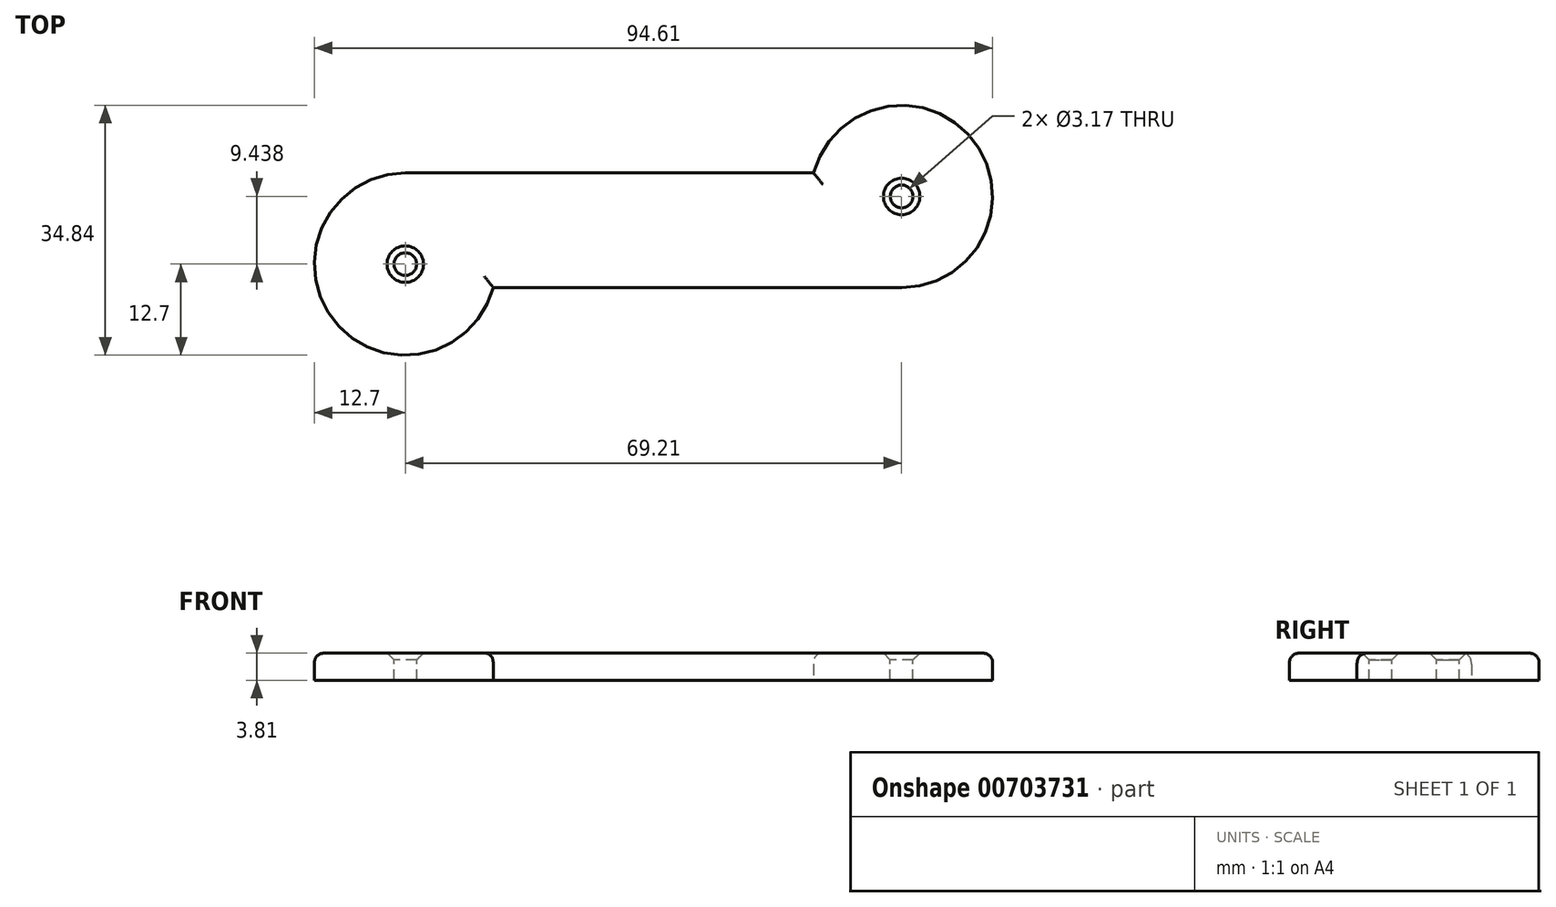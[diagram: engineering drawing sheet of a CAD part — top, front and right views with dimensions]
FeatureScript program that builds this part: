
annotation { "Feature Type Name" : "Feature", "Feature Type Description" : "" }
export const myFeature = defineFeature(function(context is Context, id is Id, definition is map)
    precondition{}
    {
        {
            var Q0;
            Q0=qCreatedBy(makeId("Top.planeOp"),FACE);
            var sketch = newSketch(context, id + "F0", { "sketchPlane" : qUnion([Q0])});
            skArc(sketch, "E0", {"start": v(0, 12.7) * mm, "mid": v(-10.07, -7.74) * mm, "end": v(12.27, -3.26) * mm});
            skArc(sketch, "E1", {"start": v(69.17, -3.26) * mm, "mid": v(79.29, 17.16) * mm, "end": v(56.94, 12.7) * mm});
            skLineSegment(sketch, "E2", {"start": v(0, 12.7) * mm, "end": v(56.94, 12.7) * mm});
            skLineSegment(sketch, "E3", {"start": v(69.25, -3.26) * mm, "end": v(12.27, -3.26) * mm});
            skSolve(sketch);
        }
        {
            var Q0;
            {var subQ0=sQuery(id+"F0.wireOp",EDGE,"E0");Q0=makeQuery(id+"F0.imprint","IMPRINT",FACE,{"disambiguationData":[TD([[makeQuery(id+"F0.imprint","IMPRINT",EDGE,{"derivedFrom":subQ0}),1.0]])]});}
            extrude(context, id + "F1", {"entities" : qUnion([Q0]), "depth" : 3.8 * mm, "offsetDistance" : 25.4 * mm});
        }
        {
            var Q0;
            Q0=makeQuery(id+"F1.opExtrude","CAP_FACE",FACE,{"disambiguationData":[OSD([sQuery(id+"F0.wireOp",EDGE,"E0"),sQuery(id+"F0.wireOp",EDGE,"E1"),sQuery(id+"F0.wireOp",EDGE,"E2"),sQuery(id+"F0.wireOp",EDGE,"E3")])],"isStart":false});
            var sketch = newSketch(context, id + "F2", { "sketchPlane" : qUnion([Q0])});
            skLineSegment(sketch, "E4", {"start": v(0, 0) * mm, "end": v(0, 23.35) * mm});
            skLineSegment(sketch, "E5", {"start": v(69.2, 9.44) * mm, "end": v(69.2, 36.96) * mm});
            skSolve(sketch);
        }
        {
            var Q0;
            Q0=sQuery(id+"F2.wireOp",VERTEX,"E4.start");
            var Q1;
            Q1=sQuery(id+"F2.wireOp",VERTEX,"E5.start");
            var Q2;
            Q2=makeQuery(id+"F1.opExtrude","SWEPT_BODY",BODY,{"disambiguationData":[OSD([sQuery(id+"F0.wireOp",EDGE,"E0"),sQuery(id+"F0.wireOp",EDGE,"E1"),sQuery(id+"F0.wireOp",EDGE,"E2"),sQuery(id+"F0.wireOp",EDGE,"E3")])]});
            hole(context, id + "F3", {"style" : HoleStyle.C_SINK, "endStyle" : HoleEndStyle.THROUGH, "holeDiameter" : 3.17 * mm, "cSinkDiameter" : 5.08 * mm, "cSinkAngle" : 90 * degree, "majorDiameter" : 6.35 * mm, "isTappedThrough" : true, "tappedDepth" : 12.7 * mm, "tapClearance" : 3, "locations" : qUnion([Q0, Q1]), "scope" : qUnion([Q2])});
        }
        {
            var Q0;
            Q0=makeQuery(id+"F1.opExtrude","CAP_EDGE",EDGE,{"disambiguationData":[OSD([sQuery(id+"F0.wireOp",EDGE,"E0")])],"isStart":false});
            var Q1;
            Q1=makeQuery(id+"F1.opExtrude","CAP_EDGE",EDGE,{"disambiguationData":[OSD([sQuery(id+"F0.wireOp",EDGE,"E3")])],"isStart":false});
            var Q2;
            Q2=makeQuery(id+"F1.opExtrude","CAP_EDGE",EDGE,{"disambiguationData":[OSD([sQuery(id+"F0.wireOp",EDGE,"E1")])],"isStart":false});
            fillet(context, id + "F4", {"entities" : qUnion([Q0, Q1, Q2]), "radius" : 1.59 * mm, "tangentPropagation" : true, "rho" : 0.5, "crossSection" : FilletCrossSection.CONIC, "allowEdgeOverflow" : false});
        }
    });
